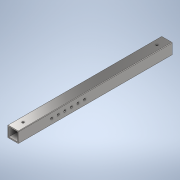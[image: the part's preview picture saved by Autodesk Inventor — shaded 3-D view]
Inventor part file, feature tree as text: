
AUTODESK INVENTOR PART (.ipt)
format: ipt  version: 2021 (Build 250183000, 183)  size: 196,096 bytes
history: native  units: mm
features: sketch x3, hole x2, extrude x1, fillet x1
ambient origin geometry x8: Origin, YZ Plane, XZ Plane, XY Plane, X Axis, Y Axis, Z Axis, Center Point
bodies: Solid1 (feature_tree)
feature tree (7):
  extrude  "Extrusion1"  Depth=50.0mm
  fillet  "Fillet1"  Radius=25.0mm
  hole  "endHoles"  [1 undecoded]
  hole  "Hole4"  [1 undecoded]
  sketch  "Sketch1"  dims[d0=50.0mm d1=50.0mm d2=25.0mm]
  sketch  "Sketch2"  dims[d3=25.0mm d4=5.0mm]
  sketch  "Sketch3"  dims[d5=700.0mm d6=0.0mm d7=2.0mm d8=45.0mm d9=0.0mm d10=45.0mm d11=0.0mm d12=10.0mm d13=6.0mm d14=4.0mm d15=2.0mm d16=90.0deg d17=8.0mm d18=0.0mm d19=400.0mm d21=0.0mm d22=0.0mm d30=30.0mm d31=30.0mm d32=30.0mm d33=30.0mm d34=30.0mm d42=10.0mm d43=6.0mm d44=4.0mm d45=2.0mm d46=90.0deg d47=8.0mm d48=20.594885mm]
note: 2 required parameter values undecoded (feature->parameter linkage not recoverable at this tier; creation-order binding heuristic only, values carry confidence <= 0.55)
